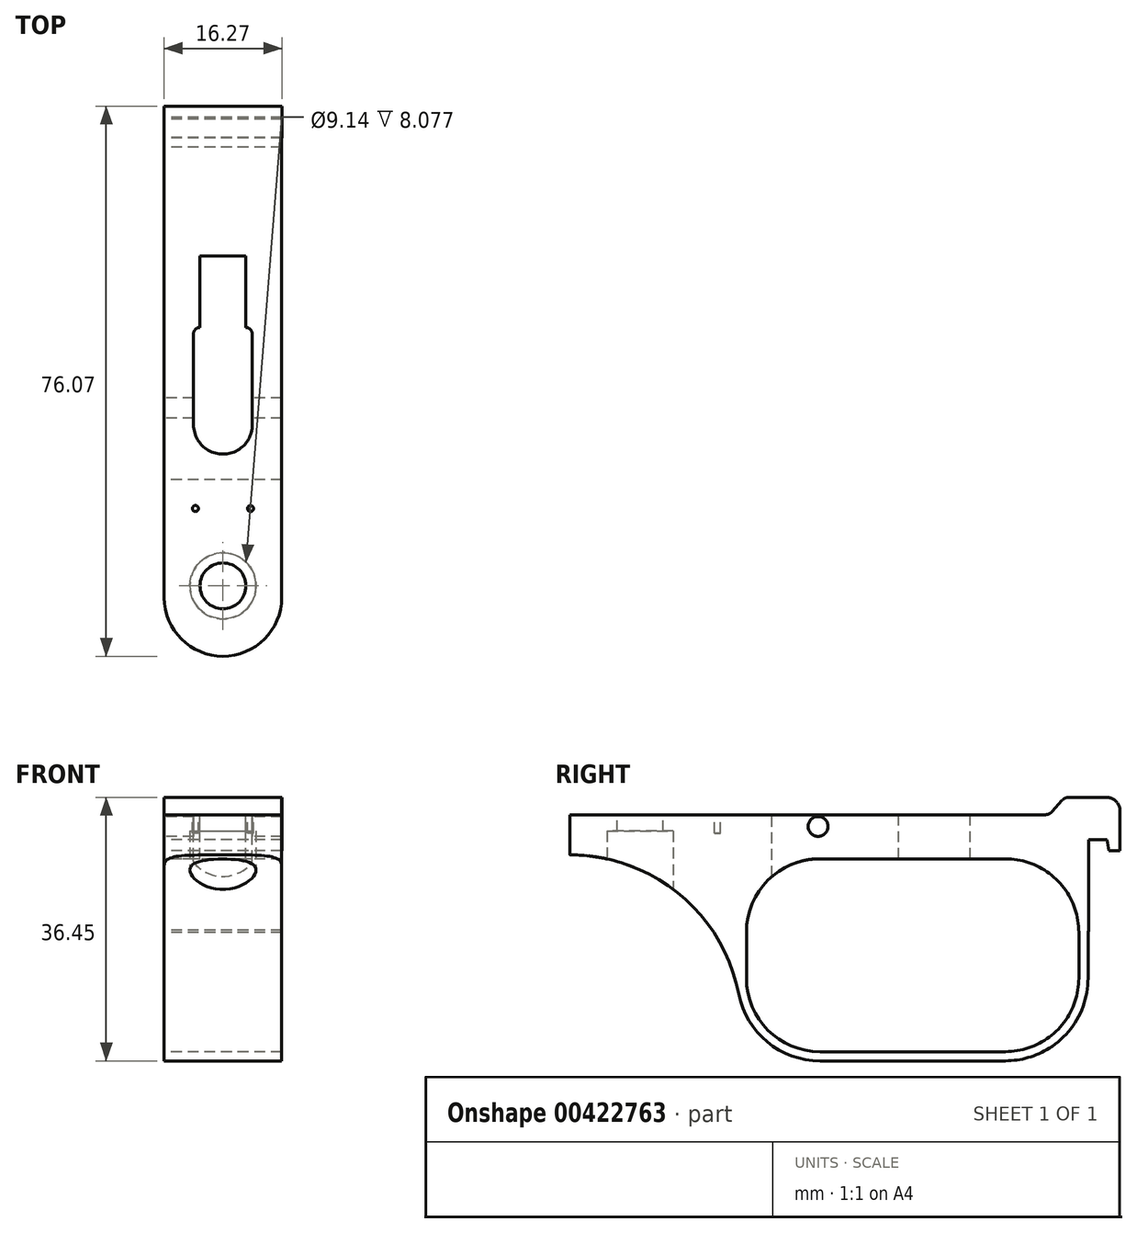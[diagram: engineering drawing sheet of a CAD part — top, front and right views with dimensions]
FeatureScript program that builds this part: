
annotation { "Feature Type Name" : "Feature", "Feature Type Description" : "" }
export const myFeature = defineFeature(function(context is Context, id is Id, definition is map)
    precondition{}
    {
        {
            var Q0;
            Q0=qCreatedBy(makeId("Top.planeOp"),FACE);
            var sketch = newSketch(context, id + "F0", { "sketchPlane" : qUnion([Q0])});
            skArc(sketch, "E0", {"start": v(-8.13, -41.11) * mm, "mid": v(0, -49.24) * mm, "end": v(8.13, -41.11) * mm});
            skCircle(sketch, "E1", {"center": v(0, -39.51) * mm, "radius": 3.18 * mm});
            skLineSegment(sketch, "E2", {"start": v(-8.13, -31.26) * mm, "end": v(8.13, -31.26) * mm});
            skCircle(sketch, "E3", {"center": v(3.81, -28.82) * mm, "radius": 0.42 * mm});
            skCircle(sketch, "E4", {"center": v(-3.8, -28.82) * mm, "radius": 0.42 * mm});
            skLineSegment(sketch, "E5", {"start": v(-8.13, -41.11) * mm, "end": v(-8.13, -31.26) * mm});
            skLineSegment(sketch, "E6", {"start": v(8.13, -41.11) * mm, "end": v(8.13, -31.26) * mm});
            skLineSegment(sketch, "E7", {"start": v(8.13, 17.06) * mm, "end": v(8.13, -31.26) * mm});
            skLineSegment(sketch, "E8", {"start": v(8.13, 17.06) * mm, "end": v(-8.13, 17.1) * mm});
            skLineSegment(sketch, "E9", {"start": v(-8.13, -31.26) * mm, "end": v(-8.13, 17.1) * mm});
            skArc(sketch, "E10.0.1.0", {"start": v(-4.06, -17.24) * mm, "mid": v(0, -21.3) * mm, "end": v(4.07, -17.23) * mm});
            skLineSegment(sketch, "E10.0.1.1", {"start": v(-4.07, -4.66) * mm, "end": v(-4.06, -17.24) * mm});
            skLineSegment(sketch, "E10.0.1.2", {"start": v(4.05, -4.66) * mm, "end": v(4.07, -17.23) * mm});
            skArc(sketch, "E10.0.1.3", {"start": v(-3.18, -3.77) * mm, "mid": v(-3.8, -4.03) * mm, "end": v(-4.07, -4.66) * mm});
            skLineSegment(sketch, "E10.0.1.4", {"start": v(-3.18, -3.77) * mm, "end": v(-3.18, 6.13) * mm});
            skArc(sketch, "E10.0.1.5", {"start": v(4.05, -4.66) * mm, "mid": v(3.8, -4.04) * mm, "end": v(3.17, -3.77) * mm});
            skLineSegment(sketch, "E10.0.1.6", {"start": v(3.17, -3.77) * mm, "end": v(3.17, 6.13) * mm});
            skLineSegment(sketch, "E10.0.1.7", {"start": v(3.17, 6.13) * mm, "end": v(-3.18, 6.13) * mm});
            skLineSegment(sketch, "E11.0", {"start": v(8.14, 26.83) * mm, "end": v(-8.13, 26.83) * mm});
            skLineSegment(sketch, "E12.0", {"start": v(8.14, 25.05) * mm, "end": v(-8.13, 25.05) * mm});
            skLineSegment(sketch, "E13.0", {"start": v(8.14, 22.51) * mm, "end": v(-8.13, 22.51) * mm});
            skLineSegment(sketch, "E14", {"start": v(-8.13, 26.83) * mm, "end": v(-8.13, 17.1) * mm});
            skLineSegment(sketch, "E15", {"start": v(8.14, 26.83) * mm, "end": v(8.13, 17.06) * mm});
            skSolve(sketch);
        }
        {
            var Q0;
            Q0=makeQuery(id+"F0.imprint","IMPRINT",FACE,{"disambiguationData":[TD([[makeQuery(id+"F0.imprint","IMPRINT",EDGE,{"derivedFrom":sQuery(id+"F0.wireOp",EDGE,"E0")}),1.0]])]});
            var Q1;
            {var subQ0=sQuery(id+"F0.wireOp",EDGE,"787198dd-bca4-4525-862f-a25401c4d90f");Q1=makeQuery(id+"F0.imprint","IMPRINT",FACE,{"disambiguationData":[TD([[makeQuery(id+"F0.imprint","IMPRINT",EDGE,{"derivedFrom":subQ0}),-1.0]])]});}
            var Q2;
            {var subQ0=sQuery(id+"F0.wireOp",EDGE,"d4342492-76fe-4402-a7e5-8071a383ea67");Q2=makeQuery(id+"F0.imprint","IMPRINT",FACE,{"disambiguationData":[TD([[makeQuery(id+"F0.imprint","IMPRINT",EDGE,{"derivedFrom":subQ0}),1.0]])]});}
            var Q3;
            Q3=makeQuery(id+"F0.imprint","IMPRINT",FACE,{"disambiguationData":[TD([[makeQuery(id+"F0.imprint","IMPRINT",EDGE,{"derivedFrom":sQuery(id+"F0.wireOp",EDGE,"14f3fbc3-f7db-4fca-b2d8-4976d205a7d3")}),1.0]])]});
            var Q4;
            Q4=makeQuery(id+"F0.imprint","IMPRINT",FACE,{"disambiguationData":[TD([[makeQuery(id+"F0.imprint","IMPRINT",EDGE,{"derivedFrom":sQuery(id+"F0.wireOp",EDGE,"E1")}),1.0]])]});
            var Q5;
            Q5=makeQuery(id+"F0.imprint","IMPRINT",FACE,{"disambiguationData":[TD([[makeQuery(id+"F0.imprint","IMPRINT",EDGE,{"derivedFrom":sQuery(id+"F0.wireOp",EDGE,"14f3fbc3-f7db-4fca-b2d8-4976d205a7d3")}),-1.0]])]});
            var Q6;
            Q6=makeQuery(id+"F0.imprint","IMPRINT",FACE,{"disambiguationData":[TD([[makeQuery(id+"F0.imprint","IMPRINT",EDGE,{"derivedFrom":sQuery(id+"F0.wireOp",EDGE,"E4")}),1.0]])]});
            var Q7;
            Q7=makeQuery(id+"F0.imprint","IMPRINT",FACE,{"disambiguationData":[TD([[makeQuery(id+"F0.imprint","IMPRINT",EDGE,{"derivedFrom":sQuery(id+"F0.wireOp",EDGE,"E3")}),1.0]])]});
            var Q8;
            Q8=makeQuery(id+"F0.imprint","IMPRINT",FACE,{"disambiguationData":[TD([[makeQuery(id+"F0.imprint","IMPRINT",EDGE,{"derivedFrom":sQuery(id+"F0.wireOp",EDGE,"2ba2d08b-a480-40bc-a49a-63f7ac935b6f")}),1.0]])]});
            var Q9;
            Q9=makeQuery(id+"F0.imprint","IMPRINT",FACE,{"disambiguationData":[TD([[makeQuery(id+"F0.imprint","IMPRINT",EDGE,{"derivedFrom":sQuery(id+"F0.wireOp",EDGE,"E2")}),1.0]])]});
            var Q10;
            Q10=makeQuery(id+"F0.imprint","IMPRINT",FACE,{"disambiguationData":[TD([[makeQuery(id+"F0.imprint","IMPRINT",EDGE,{"derivedFrom":sQuery(id+"F0.wireOp",EDGE,"E10.0.1.0")}),1.0]])]});
            var Q11;
            {var subQ0=sQuery(id+"F0.wireOp",EDGE,"E8");Q11=makeQuery(id+"F0.imprint","IMPRINT",FACE,{"disambiguationData":[TD([[makeQuery(id+"F0.imprint","IMPRINT",EDGE,{"derivedFrom":subQ0}),-1.0]])]});}
            extrude(context, id + "F1", {"entities" : qUnion([Q0, Q1, Q2, Q3, Q4, Q5, Q6, Q7, Q8, Q9, Q10, Q11]), "oppositeDirection" : true, "depth" : 34.54 * mm, "offsetDistance" : 25.4 * mm});
        }
        {
            var Q0;
            {var subQ0=sQuery(id+"F0.wireOp",EDGE,"E8");Q0=makeQuery(id+"F0.imprint","IMPRINT",FACE,{"disambiguationData":[TD([[makeQuery(id+"F0.imprint","IMPRINT",EDGE,{"derivedFrom":subQ0}),-1.0]])]});}
            var Q1;
            {var subQ0=sQuery(id+"F0.wireOp",EDGE,"E14");var subQ1=sQuery(id+"F0.wireOp",EDGE,"E12.0");var subQ2=makeQuery(id+"F0.imprint","INTERSECT",VERTEX,{"derivedFrom":[subQ1,subQ0]});Q1=makeQuery(id+"F0.imprint","IMPRINT",FACE,{"disambiguationData":[TD([[makeQuery(id+"F0.imprint","IMPRINT",EDGE,{"disambiguationData":[TD([[subQ2,1.0]])],"derivedFrom":subQ1}),1.0]])]});}
            var Q2;
            {var subQ0=sQuery(id+"F0.wireOp",EDGE,"E11.0");Q2=makeQuery(id+"F0.imprint","IMPRINT",FACE,{"disambiguationData":[TD([[makeQuery(id+"F0.imprint","IMPRINT",EDGE,{"derivedFrom":subQ0}),1.0]])]});}
            extrude(context, id + "F2", {"entities" : qUnion([Q0, Q1, Q2]), "operationType" : NewBodyOperationType.ADD, "depth" : 2.41 * mm, "offsetDistance" : 25.4 * mm});
        }
        {
            var Q0;
            {var subQ0=sQuery(id+"F0.wireOp",EDGE,"E11.0");Q0=makeQuery(id+"F0.imprint","IMPRINT",FACE,{"disambiguationData":[TD([[makeQuery(id+"F0.imprint","IMPRINT",EDGE,{"derivedFrom":subQ0}),1.0]])]});}
            extrude(context, id + "F3", {"entities" : qUnion([Q0]), "operationType" : NewBodyOperationType.ADD, "oppositeDirection" : true, "depth" : 4.95 * mm, "offsetDistance" : 25.4 * mm});
        }
        {
            var Q0;
            {var subQ0=sQuery(id+"F0.wireOp",EDGE,"E14");var subQ1=sQuery(id+"F0.wireOp",EDGE,"E12.0");var subQ2=makeQuery(id+"F0.imprint","INTERSECT",VERTEX,{"derivedFrom":[subQ1,subQ0]});Q0=makeQuery(id+"F0.imprint","IMPRINT",FACE,{"disambiguationData":[TD([[makeQuery(id+"F0.imprint","IMPRINT",EDGE,{"disambiguationData":[TD([[subQ2,1.0]])],"derivedFrom":subQ1}),1.0]])]});}
            extrude(context, id + "F4", {"entities" : qUnion([Q0]), "operationType" : NewBodyOperationType.ADD, "oppositeDirection" : true, "depth" : 3.43 * mm, "offsetDistance" : 25.4 * mm});
        }
        {
            var Q0;
            Q0=makeQuery(id+"F3.opExtrude","CAP_EDGE",EDGE,{"disambiguationData":[OSD([sQuery(id+"F0.wireOp",EDGE,"E12.0")])],"isStart":false});
            chamfer(context, id + "F5", {"entities" : qUnion([Q0]), "chamferType" : ChamferType.TWO_OFFSETS, "width1" : 0.25 * mm, "oppositeDirection" : false, "width2" : 1.52 * mm, "tangentPropagation" : true});
        }
        {
            var Q0;
            Q0=makeQuery(id+"F2.opExtrude","CAP_EDGE",EDGE,{"disambiguationData":[OSD([sQuery(id+"F0.wireOp",EDGE,"E11.0")])],"isStart":false});
            fillet(context, id + "F6", {"entities" : qUnion([Q0]), "radius" : 1.9 * mm, "tangentPropagation" : true, "allowEdgeOverflow" : false});
        }
        {
            var Q0;
            Q0=makeQuery(id+"F2.opExtrude","CAP_EDGE",EDGE,{"disambiguationData":[OSD([sQuery(id+"F0.wireOp",EDGE,"7dc91bf6-54e8-47e1-96ad-06bf4c2fe70e")])],"isStart":false});
            var Q1;
            Q1=makeQuery(id+"F2.opExtrude","CAP_EDGE",EDGE,{"disambiguationData":[OSD([sQuery(id+"F0.wireOp",EDGE,"E8")])],"isStart":false});
            chamfer(context, id + "F7", {"entities" : qUnion([Q0, Q1]), "chamferType" : ChamferType.TWO_OFFSETS, "width1" : 2.41 * mm, "oppositeDirection" : false, "width2" : 2.16 * mm, "tangentPropagation" : true});
        }
        {
            var Q0;
            {var subQ0=sQuery(id+"F0.wireOp",EDGE,"E8");Q0=makeQuery(id+"F7.opChamfer","BLEND_EDGE",EDGE,{"blendedFrom":[makeQuery(id+"F2.opExtrude","CAP_EDGE",EDGE,{"disambiguationData":[OSD([subQ0])],"isStart":false}),makeQuery(id+"F2.opExtrude","CAP_FACE",FACE,{"disambiguationData":[OSD([sQuery(id+"F0.wireOp",EDGE,"2ba2d08b-a480-40bc-a49a-63f7ac935b6f"),sQuery(id+"F0.wireOp",EDGE,"51bec652-feed-41d8-be01-f610db7fccb2"),sQuery(id+"F0.wireOp",EDGE,"d2ff1fdb-81b8-4d5b-8183-54ec4aa39f79"),subQ0,sQuery(id+"F0.wireOp",EDGE,"e9b4325e-633b-4c99-a355-854da90ad89a"),sQuery(id+"F0.wireOp",EDGE,"e27526e9-fc86-41b9-a4bb-bd6bf49bbd22"),sQuery(id+"F0.wireOp",EDGE,"4f54c5d3-c9e5-4447-8428-f8bf015c2b1e"),sQuery(id+"F0.wireOp",EDGE,"8417e815-5c9d-4c69-be65-91e07e5c03b4")])],"isStart":false})],"blendedInto":[makeQuery(id+"F2.opExtrude","CAP_FACE",FACE,{"disambiguationData":[OSD([sQuery(id+"F0.wireOp",EDGE,"2ba2d08b-a480-40bc-a49a-63f7ac935b6f"),sQuery(id+"F0.wireOp",EDGE,"51bec652-feed-41d8-be01-f610db7fccb2"),sQuery(id+"F0.wireOp",EDGE,"d2ff1fdb-81b8-4d5b-8183-54ec4aa39f79"),subQ0,sQuery(id+"F0.wireOp",EDGE,"e9b4325e-633b-4c99-a355-854da90ad89a"),sQuery(id+"F0.wireOp",EDGE,"e27526e9-fc86-41b9-a4bb-bd6bf49bbd22"),sQuery(id+"F0.wireOp",EDGE,"4f54c5d3-c9e5-4447-8428-f8bf015c2b1e"),sQuery(id+"F0.wireOp",EDGE,"8417e815-5c9d-4c69-be65-91e07e5c03b4")])],"isStart":false})]});}
            fillet(context, id + "F8", {"entities" : qUnion([Q0]), "radius" : 1.27 * mm, "tangentPropagation" : true, "allowEdgeOverflow" : false});
        }
        {
            var Q0;
            Q0=makeQuery(id+"F7.opChamfer","BLEND_EDGE",EDGE,{"blendedFrom":[makeQuery(id+"F2.opExtrude","CAP_EDGE",EDGE,{"disambiguationData":[OSD([sQuery(id+"F0.wireOp",EDGE,"E8")])],"isStart":false}),makeQuery(id+"F1.opExtrude","CAP_FACE",FACE,{"disambiguationData":[OSD([sQuery(id+"F0.wireOp",EDGE,"E0"),sQuery(id+"F0.wireOp",EDGE,"E5"),sQuery(id+"F0.wireOp",EDGE,"E6"),sQuery(id+"F0.wireOp",EDGE,"E7"),sQuery(id+"F0.wireOp",EDGE,"2ba2d08b-a480-40bc-a49a-63f7ac935b6f"),sQuery(id+"F0.wireOp",EDGE,"3f80772e-eff1-4091-b0e4-309ee9bfc49d"),sQuery(id+"F0.wireOp",EDGE,"E9"),sQuery(id+"F0.wireOp",EDGE,"e27526e9-fc86-41b9-a4bb-bd6bf49bbd22")])],"isStart":true})],"blendedInto":[makeQuery(id+"F1.opExtrude","CAP_FACE",FACE,{"disambiguationData":[OSD([sQuery(id+"F0.wireOp",EDGE,"E0"),sQuery(id+"F0.wireOp",EDGE,"E5"),sQuery(id+"F0.wireOp",EDGE,"E6"),sQuery(id+"F0.wireOp",EDGE,"E7"),sQuery(id+"F0.wireOp",EDGE,"2ba2d08b-a480-40bc-a49a-63f7ac935b6f"),sQuery(id+"F0.wireOp",EDGE,"3f80772e-eff1-4091-b0e4-309ee9bfc49d"),sQuery(id+"F0.wireOp",EDGE,"E9"),sQuery(id+"F0.wireOp",EDGE,"e27526e9-fc86-41b9-a4bb-bd6bf49bbd22")])],"isStart":true})]});
            fillet(context, id + "F9", {"entities" : qUnion([Q0]), "radius" : 1.27 * mm, "tangentPropagation" : true, "allowEdgeOverflow" : false});
        }
        {
            var Q0;
            {var subQ0=sQuery(id+"F0.wireOp",EDGE,"4f54c5d3-c9e5-4447-8428-f8bf015c2b1e");var subQ1=sQuery(id+"F0.wireOp",EDGE,"8417e815-5c9d-4c69-be65-91e07e5c03b4");var subQ2=sQuery(id+"F0.wireOp",EDGE,"e27526e9-fc86-41b9-a4bb-bd6bf49bbd22");Q0=makeQuery(id+"F4.boolean.opBoolean","MERGE",FACE,{"derivedFrom":[makeQuery(id+"F3.boolean.opBoolean","MERGE",FACE,{"derivedFrom":[makeQuery(id+"F2.boolean.opBoolean","MERGE",FACE,{"derivedFrom":[makeQuery(id+"F1.opExtrude","SWEPT_FACE",FACE,{"disambiguationData":[OSD([sQuery(id+"F0.wireOp",EDGE,"E9"),subQ2])]}),makeQuery(id+"F2.opExtrude","SWEPT_FACE",FACE,{"disambiguationData":[OSD([subQ2,subQ0,subQ1])]})]}),makeQuery(id+"F3.opExtrude","SWEPT_FACE",FACE,{"disambiguationData":[OSD([subQ1])]})]}),makeQuery(id+"F4.opExtrude","SWEPT_FACE",FACE,{"disambiguationData":[OSD([subQ0])]})]});}
            var sketch = newSketch(context, id + "F10", { "sketchPlane" : qUnion([Q0])});
            skCircle(sketch, "E16.1.0.20", {"center": v(14.92, -1.63) * mm, "radius": 1.37 * mm});
            skLineSegment(sketch, "E17.0.1.2", {"start": v(26.1, -5.56) * mm, "end": v(55.09, -5.56) * mm});
            skArc(sketch, "E17.0.1.5", {"start": v(14.67, -34.04) * mm, "mid": v(22.75, -30.69) * mm, "end": v(26.1, -22.6) * mm});
            skLineSegment(sketch, "E17.0.1.6", {"start": v(14.67, -34.04) * mm, "end": v(-10.98, -34.04) * mm});
            skLineSegment(sketch, "E17.0.1.7", {"start": v(-23.18, -34.54) * mm, "end": v(55.09, -34.54) * mm});
            skLineSegment(sketch, "E17.0.1.8", {"start": v(-10.98, -32.77) * mm, "end": v(14.67, -32.77) * mm});
            skArc(sketch, "E17.0.1.9", {"start": v(24.83, -22.6) * mm, "mid": v(21.85, -29.8) * mm, "end": v(14.67, -32.77) * mm});
            skLineSegment(sketch, "E17.0.1.10", {"start": v(24.83, -16.26) * mm, "end": v(24.83, -22.6) * mm});
            skArc(sketch, "E17.0.1.11", {"start": v(14.67, -6.1) * mm, "mid": v(21.85, -9.07) * mm, "end": v(24.83, -16.26) * mm});
            skLineSegment(sketch, "E17.0.1.12", {"start": v(14.67, -6.1) * mm, "end": v(-10.98, -6.1) * mm});
            skArc(sketch, "E17.0.1.13", {"start": v(-10.98, -6.1) * mm, "mid": v(-18.17, -9.07) * mm, "end": v(-21.14, -16.26) * mm});
            skLineSegment(sketch, "E17.0.1.14", {"start": v(-21.14, -16.26) * mm, "end": v(-21.14, -22.6) * mm});
            skArc(sketch, "E17.0.1.15", {"start": v(-21.14, -22.6) * mm, "mid": v(-18.17, -29.8) * mm, "end": v(-10.98, -32.77) * mm});
            skArc(sketch, "E17.0.1.16", {"start": v(-22.41, -22.6) * mm, "mid": v(-19.07, -30.69) * mm, "end": v(-10.98, -34.04) * mm});
            skLineSegment(sketch, "E17.0.1.17", {"start": v(-23.18, -14.1) * mm, "end": v(-23.18, -34.54) * mm});
            skLineSegment(sketch, "E17.0.1.18", {"start": v(-22.41, -16.26) * mm, "end": v(-22.41, -22.6) * mm});
            skLineSegment(sketch, "E17.0.1.19", {"start": v(-23.18, -14.1) * mm, "end": v(-22.41, -16.26) * mm});
            skLineSegment(sketch, "E18", {"start": v(55.09, -5.56) * mm, "end": v(55.09, -34.54) * mm});
            skLineSegment(sketch, "E19", {"start": v(26.1, -5.56) * mm, "end": v(26.1, -22.6) * mm});
            skSolve(sketch);
        }
        {
            var Q0;
            Q0=qSketchRegion(id+"F10",true);
            extrude(context, id + "F11", {"entities" : qUnion([Q0]), "operationType" : NewBodyOperationType.REMOVE, "endBound" : BoundingType.THROUGH_ALL, "oppositeDirection" : true, "depth" : 25.4 * mm, "offsetDistance" : 25.4 * mm});
        }
        {
            var Q0;
            Q0=makeQuery(id+"F0.imprint","IMPRINT",FACE,{"disambiguationData":[TD([[makeQuery(id+"F0.imprint","IMPRINT",EDGE,{"derivedFrom":sQuery(id+"F0.wireOp",EDGE,"E1")}),1.0]])]});
            extrude(context, id + "F12", {"entities" : qUnion([Q0]), "operationType" : NewBodyOperationType.REMOVE, "endBound" : BoundingType.THROUGH_ALL, "oppositeDirection" : true, "depth" : 25.4 * mm, "offsetDistance" : 25.4 * mm});
        }
        {
            var Q0;
            Q0=makeQuery(id+"F0.imprint","IMPRINT",FACE,{"disambiguationData":[TD([[makeQuery(id+"F0.imprint","IMPRINT",EDGE,{"derivedFrom":sQuery(id+"F0.wireOp",EDGE,"14f3fbc3-f7db-4fca-b2d8-4976d205a7d3")}),1.0]])]});
            var Q1;
            Q1=makeQuery(id+"F0.imprint","IMPRINT",FACE,{"disambiguationData":[TD([[makeQuery(id+"F0.imprint","IMPRINT",EDGE,{"derivedFrom":sQuery(id+"F0.wireOp",EDGE,"E10.0.1.0")}),1.0]])]});
            extrude(context, id + "F13", {"entities" : qUnion([Q0, Q1]), "operationType" : NewBodyOperationType.REMOVE, "oppositeDirection" : true, "depth" : 8.9 * mm, "offsetDistance" : 25.4 * mm});
        }
        {
            var Q0;
            Q0=makeQuery(id+"F0.imprint","IMPRINT",FACE,{"disambiguationData":[TD([[makeQuery(id+"F0.imprint","IMPRINT",EDGE,{"derivedFrom":sQuery(id+"F0.wireOp",EDGE,"E4")}),1.0]])]});
            var Q1;
            Q1=makeQuery(id+"F0.imprint","IMPRINT",FACE,{"disambiguationData":[TD([[makeQuery(id+"F0.imprint","IMPRINT",EDGE,{"derivedFrom":sQuery(id+"F0.wireOp",EDGE,"E3")}),1.0]])]});
            extrude(context, id + "F14", {"entities" : qUnion([Q0, Q1]), "operationType" : NewBodyOperationType.REMOVE, "oppositeDirection" : true, "depth" : 2.54 * mm, "offsetDistance" : 25.4 * mm});
        }
        {
            var Q0;
            Q0=makeQuery(id+"F11.boolean.opBoolean","COPY",FACE,{"derivedFrom":makeQuery(id+"F11.opExtrude","SWEPT_FACE",FACE,{"disambiguationData":[OSD([sQuery(id+"F10.wireOp",EDGE,"E17.0.1.2")])]})});
            var sketch = newSketch(context, id + "F15", { "sketchPlane" : qUnion([Q0])});
            skCircle(sketch, "E20", {"center": v(0, 39.51) * mm, "radius": 4.57 * mm});
            skSolve(sketch);
        }
        {
            var Q0;
            Q0=makeQuery(id+"F15.imprint","IMPRINT",FACE,{"disambiguationData":[TD([[makeQuery(id+"F15.imprint","IMPRINT",EDGE,{"derivedFrom":sQuery(id+"F15.wireOp",EDGE,"E20")}),1.0]])]});
            extrude(context, id + "F16", {"entities" : qUnion([Q0]), "operationType" : NewBodyOperationType.REMOVE, "oppositeDirection" : true, "depth" : 3.3 * mm, "offsetDistance" : 25.4 * mm});
        }
        {
            var Q0;
            Q0=makeQuery(id+"F11.boolean.opBoolean","COPY",EDGE,{"derivedFrom":makeQuery(id+"F11.opExtrude","SWEPT_EDGE",EDGE,{"disambiguationData":[OSD([sQuery(id+"F10.wireOp",EDGE,"E17.0.1.2"),sQuery(id+"F10.wireOp",EDGE,"E19")])]})});
            fillet(context, id + "F17", {"entities" : qUnion([Q0]), "radius" : 23.79 * mm, "tangentPropagation" : true, "allowEdgeOverflow" : false});
        }
    });
